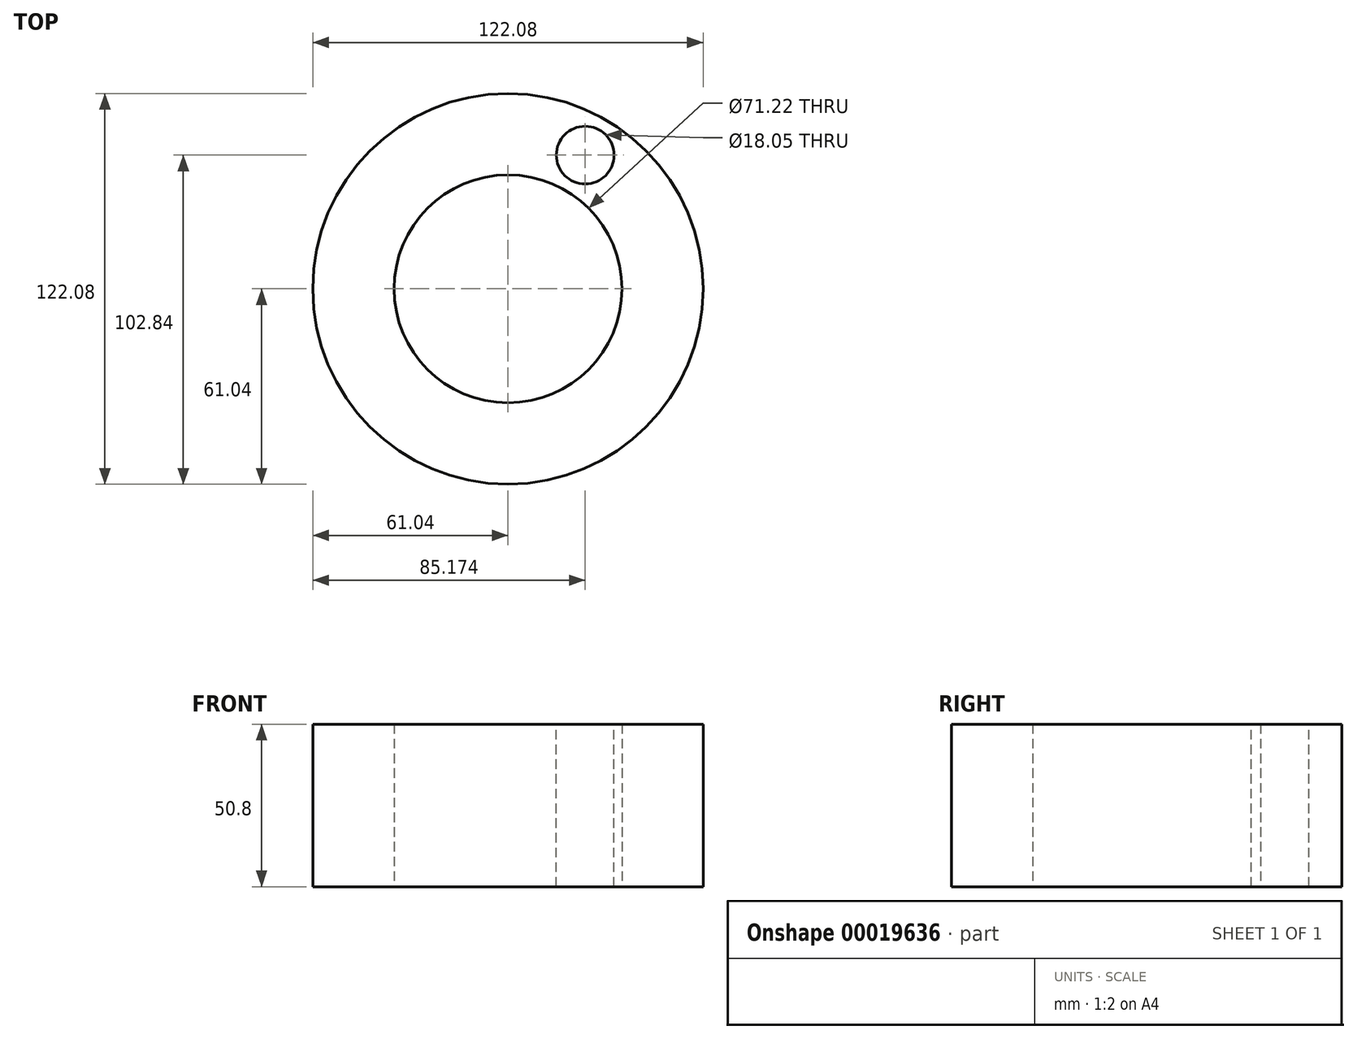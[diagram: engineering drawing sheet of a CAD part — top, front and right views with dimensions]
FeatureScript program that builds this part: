
annotation { "Feature Type Name" : "Feature", "Feature Type Description" : "" }
export const myFeature = defineFeature(function(context is Context, id is Id, definition is map)
    precondition{}
    {
        {
            var Q0;
            Q0=qCreatedBy(makeId("Top.planeOp"),FACE);
            var sketch = newSketch(context, id + "F0", { "sketchPlane" : qUnion([Q0])});
            skCircle(sketch, "E0", {"center": v(0, 0) * mm, "radius": 61.04 * mm});
            skCircle(sketch, "E1", {"center": v(0, 0) * mm, "radius": 35.61 * mm});
            skSolve(sketch);
        }
        {
            var Q0;
            Q0=makeQuery(id+"F0.imprint","IMPRINT",FACE,{"disambiguationData":[TD([[makeQuery(id+"F0.imprint","IMPRINT",EDGE,{"derivedFrom":sQuery(id+"F0.wireOp",EDGE,"E0")}),1.0]])]});
            extrude(context, id + "F1", {"entities" : qUnion([Q0]), "depth" : 50.8 * mm});
        }
        {
            var Q0;
            Q0=makeQuery(id+"F1.opExtrude","CAP_FACE",FACE,{"disambiguationData":[OSD([sQuery(id+"F0.wireOp",EDGE,"E0"),sQuery(id+"F0.wireOp",EDGE,"E1")])],"isStart":false});
            var sketch = newSketch(context, id + "F2", { "sketchPlane" : qUnion([Q0])});
            skCircle(sketch, "E2", {"center": v(24.13, 41.8) * mm, "radius": 9.02 * mm});
            skSolve(sketch);
        }
        {
            var Q0;
            Q0=makeQuery(id+"F2.imprint","IMPRINT",FACE,{"disambiguationData":[TD([[makeQuery(id+"F2.imprint","IMPRINT",EDGE,{"derivedFrom":sQuery(id+"F2.wireOp",EDGE,"E2")}),1.0]])]});
            extrude(context, id + "F3", {"entities" : qUnion([Q0]), "operationType" : NewBodyOperationType.REMOVE, "oppositeDirection" : true, "depth" : 50.8 * mm});
        }
    });
